# Revit family: Hitachi_airCloud-PRO-Gateway_LOD400
name_source: partatom
category: Equipement de génie climatique
revit_build: Autodesk Revit 2018 (Build: 20181015_0930(x64)
units: mm (PartAtom-declared; Revit-internal decimal feet)

## family parameters
Basée sur le plan de construction = Non
Classification = Aucun
Cote de connecteur circulaire = Utiliser le diamètre
Couper avec des vides une fois chargée = Non
Partagée = Non
Point de calcul de pièce = Non
Toujours verticalement = Oui
Type d'élément = Normal

## types (1)
- HC-IOTGW
    BC_OBJECT_ID = 219733
    BC_OBJECT_VERSION = #2
    BC_VARIANT_ID = 582326
    Box = Box
    Color = White
    Communication Type = HLINK and TCP/IP
    Fabricant = Hitachi Air Conditioning Europe SAS
    Face = Face
    Frequency = 50 Hz
    IP Protection = 0X
    LED = LED
    Manufacturer Product Link = -
    Mass = 0.65 kg
    MasterFormat = Electric and Electronic Control System for HVAC
    Masterformat Code = 23 09 33
    Maximum Operating Temperature = 50 °C
    Minimum Operating Temperature = -10 °C
    Modèle = airCloud Pro HC-IOTGW
    Nominal Current = 0 A
    Nominal Voltage = 230 V
    OmniClass code = 23-27 15 23 11
    OmniClass description = HVAC Main Control Panels
    Overall depth = 52 mm
    Overall height = 201 mm
    Overall width = 146 mm
    Product Code = 60063203
    Reference = HC-IOTGW
    Uniformat = Other Controls & Instrumentation
    Uniformat code = D306002
